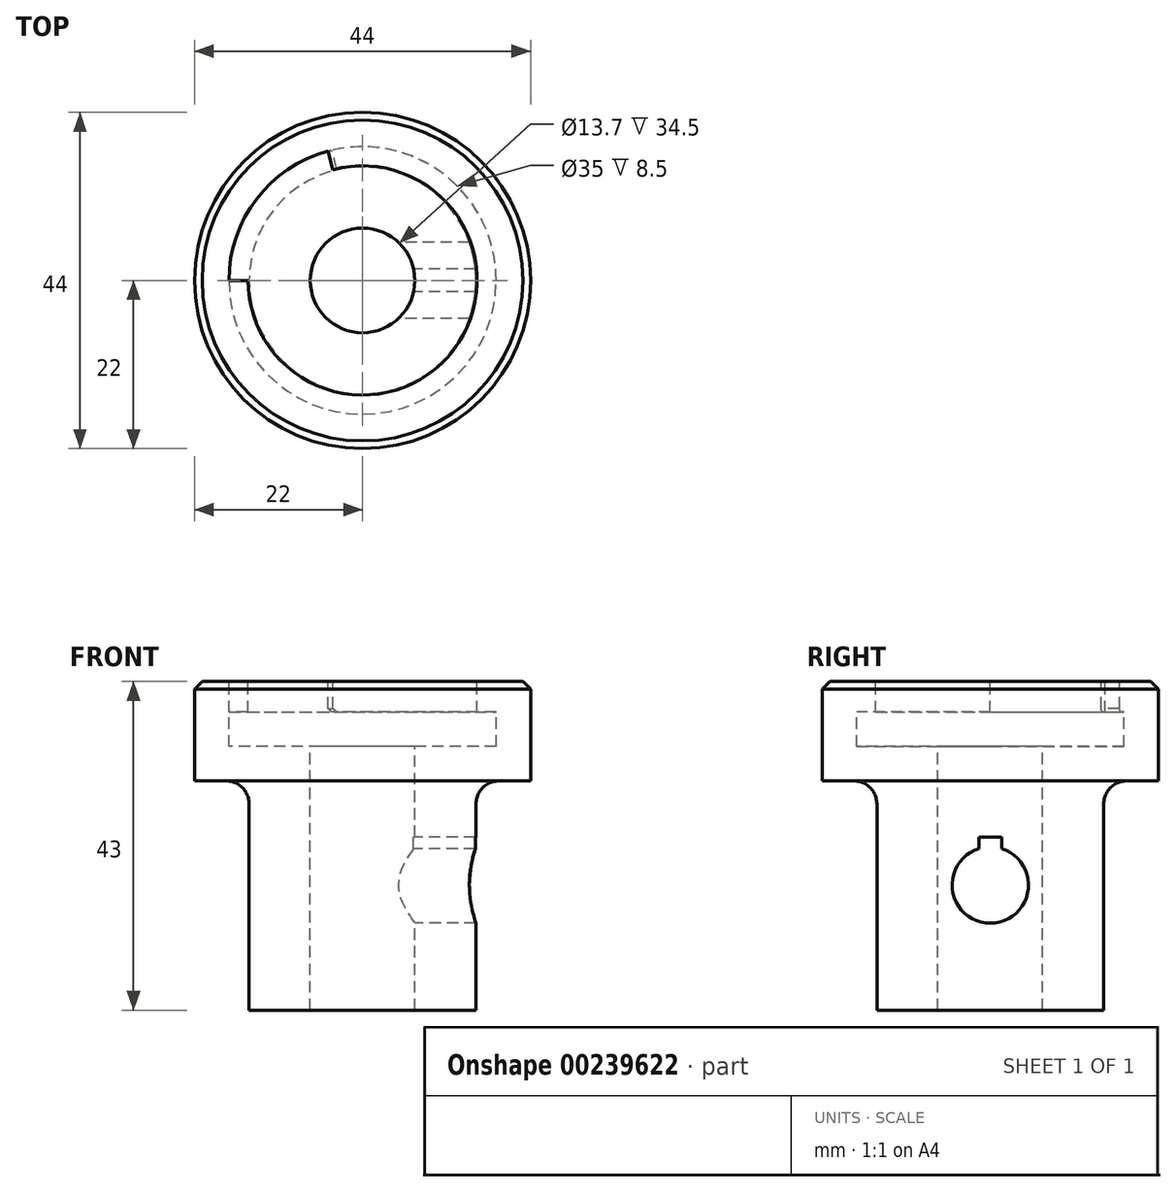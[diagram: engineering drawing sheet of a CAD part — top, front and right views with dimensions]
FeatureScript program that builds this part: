
annotation { "Feature Type Name" : "Feature", "Feature Type Description" : "" }
export const myFeature = defineFeature(function(context is Context, id is Id, definition is map)
    precondition{}
    {
        {
            var Q0;
            Q0=qCreatedBy(makeId("Front.planeOp"),FACE);
            var sketch = newSketch(context, id + "F0", { "sketchPlane" : qUnion([Q0])});
            skLineSegment(sketch, "E0", {"start": v(-22, 30) * mm, "end": v(-22, 43) * mm});
            skLineSegment(sketch, "E1", {"start": v(-22, 43) * mm, "end": v(-15, 43) * mm});
            skLineSegment(sketch, "E2", {"start": v(-15, 43) * mm, "end": v(-15, 39) * mm});
            skLineSegment(sketch, "E3", {"start": v(-15, 39) * mm, "end": v(-17.5, 39) * mm});
            skLineSegment(sketch, "E4", {"start": v(-17.5, 39) * mm, "end": v(-17.5, 34.5) * mm});
            skLineSegment(sketch, "E5", {"start": v(-17.5, 34.5) * mm, "end": v(-6.85, 34.5) * mm});
            skLineSegment(sketch, "E6", {"start": v(-6.85, 34.5) * mm, "end": v(-6.85, 0) * mm});
            skLineSegment(sketch, "E7", {"start": v(0, 7.97) * mm, "end": v(0, -2.06) * mm});
            skLineSegment(sketch, "E8", {"start": v(-14.85, 0) * mm, "end": v(-6.85, 0) * mm});
            skLineSegment(sketch, "E9", {"start": v(-22, 30) * mm, "end": v(-17.85, 30) * mm});
            skLineSegment(sketch, "E10", {"start": v(-14.85, 27) * mm, "end": v(-14.85, 0) * mm});
            skPoint(sketch, "E11.visualSharp", {"position": v(-14.85, 30) * mm});
            skArc(sketch, "E11.filletArc", {"start": v(-14.85, 27) * mm, "mid": v(-15.73, 29.12) * mm, "end": v(-17.85, 30) * mm});
            skSolve(sketch);
        }
        {
            var Q0;
            Q0 = qSketchRegion(id + "F0", true);
            var Q1;
            Q1=sQuery(id+"F0.wireOp",EDGE,"E7");
            revolve(context, id + "F1", {"entities" : qUnion([Q0]), "axis" : qUnion([Q1]), "revolveType" : RevolveType.FULL});
        }
        {
            var Q0;
            Q0=makeQuery(id+"F1.opRevolve","SWEPT_FACE",FACE,{"disambiguationData":[OSD([sQuery(id+"F0.wireOp",EDGE,"E1")])]});
            var sketch = newSketch(context, id + "F2", { "sketchPlane" : qUnion([Q0])});
            skCircle(sketch, "E12", {"center": v(0, 0) * mm, "radius": 17.5 * mm});
            skLineSegment(sketch, "E13", {"start": v(-15, 0) * mm, "end": v(-17.5, 0) * mm});
            skLineSegment(sketch, "E14", {"start": v(-3.88, 14.49) * mm, "end": v(-4.53, 16.9) * mm});
            skSolve(sketch);
        }
        {
            var Q0;
            {var subQ0=sQuery(id+"F2.wireOp",EDGE,"E13");Q0=makeQuery(id+"F2.imprint","IMPRINT",FACE,{"disambiguationData":[TD([[makeQuery(id+"F2.imprint","IMPRINT",EDGE,{"derivedFrom":subQ0}),-1.0]])]});}
            extrude(context, id + "F3", {"entities" : qUnion([Q0]), "operationType" : NewBodyOperationType.REMOVE, "oppositeDirection" : true, "depth" : 4.5 * mm});
        }
        {
            var Q0;
            Q0=makeQuery(id+"F1.opRevolve","SWEPT_EDGE",EDGE,{"disambiguationData":[OSD([sQuery(id+"F0.wireOp",EDGE,"E0"),sQuery(id+"F0.wireOp",EDGE,"E1")])]});
            chamfer(context, id + "F4", {"entities" : qUnion([Q0]), "width" : 1 * mm, "tangentPropagation" : true});
        }
        {
            var Q0;
            {var subQ0=sQuery(id+"F2.wireOp",EDGE,"E14");Q0=makeQuery(id+"Fz9Qw8WGeFSAcPO_1.2.F3.boolean.opBoolean","INTERSECT",EDGE,{"derivedFrom":[makeQuery(id+"Fz9Qw8WGeFSAcPO_1.1.F3.boolean.opBoolean","SPLIT",FACE,{"disambiguationData":[TD([makeQuery(id+"F3.boolean.opBoolean","COPY",FACE,{"derivedFrom":makeQuery(id+"F3.opExtrude","SWEPT_FACE",FACE,{"disambiguationData":[OSD([subQ0])]})})])],"derivedFrom":makeQuery(id+"F1.opRevolve","SWEPT_FACE",FACE,{"disambiguationData":[OSD([sQuery(id+"F0.wireOp",EDGE,"E3")])]})}),makeQuery(id+"Fz9Qw8WGeFSAcPO_1.2.F3.opExtrude","SWEPT_FACE",FACE,{"disambiguationData":[OSD([subQ0])]})]});}
            var Q1;
            {var subQ0=sQuery(id+"F2.wireOp",EDGE,"E14");var subQ1=makeQuery(id+"F3.boolean.opBoolean","COPY",FACE,{"derivedFrom":makeQuery(id+"F3.opExtrude","SWEPT_FACE",FACE,{"disambiguationData":[OSD([subQ0])]})});Q1=makeQuery(id+"Fz9Qw8WGeFSAcPO_1.3.F3.boolean.opBoolean","INTERSECT",EDGE,{"derivedFrom":[makeQuery(id+"Fz9Qw8WGeFSAcPO_1.2.F3.boolean.opBoolean","SPLIT",FACE,{"disambiguationData":[TD([subQ1])],"derivedFrom":makeQuery(id+"Fz9Qw8WGeFSAcPO_1.1.F3.boolean.opBoolean","SPLIT",FACE,{"disambiguationData":[TD([subQ1])],"derivedFrom":makeQuery(id+"F1.opRevolve","SWEPT_FACE",FACE,{"disambiguationData":[OSD([sQuery(id+"F0.wireOp",EDGE,"E3")])]})})}),makeQuery(id+"Fz9Qw8WGeFSAcPO_1.3.F3.opExtrude","SWEPT_FACE",FACE,{"disambiguationData":[OSD([subQ0])]})]});}
            var Q2;
            Q2=makeQuery(id+"F3.boolean.opBoolean","INTERSECT",EDGE,{"derivedFrom":[makeQuery(id+"F1.opRevolve","SWEPT_FACE",FACE,{"disambiguationData":[OSD([sQuery(id+"F0.wireOp",EDGE,"E3")])]}),makeQuery(id+"F3.opExtrude","SWEPT_FACE",FACE,{"disambiguationData":[OSD([sQuery(id+"F2.wireOp",EDGE,"E14")])]})]});
            var Q3;
            Q3=makeQuery(id+"Fz9Qw8WGeFSAcPO_1.1.F3.boolean.opBoolean","INTERSECT",EDGE,{"derivedFrom":[makeQuery(id+"F1.opRevolve","SWEPT_FACE",FACE,{"disambiguationData":[OSD([sQuery(id+"F0.wireOp",EDGE,"E3")])]}),makeQuery(id+"Fz9Qw8WGeFSAcPO_1.1.F3.opExtrude","SWEPT_FACE",FACE,{"disambiguationData":[OSD([sQuery(id+"F2.wireOp",EDGE,"E14")])]})]});
            chamfer(context, id + "F5", {"entities" : qUnion([Q0, Q1, Q2, Q3]), "width" : 0.5 * mm, "tangentPropagation" : true});
        }
        {
            var Q0;
            Q0=qCreatedBy(makeId("Right.planeOp"),FACE);
            var sketch = newSketch(context, id + "F6", { "sketchPlane" : qUnion([Q0])});
            skCircle(sketch, "E15", {"center": v(0, 16.37) * mm, "radius": 5 * mm});
            skSolve(sketch);
        }
        {
            var Q0;
            Q0 = qSketchRegion(id + "F6", true);
            extrude(context, id + "F7", {"entities" : qUnion([Q0]), "operationType" : NewBodyOperationType.REMOVE, "endBound" : BoundingType.THROUGH_ALL, "depth" : 25 * mm});
        }
        {
            var Q0;
            Q0=qCreatedBy(makeId("Right.planeOp"),FACE);
            var sketch = newSketch(context, id + "F8", { "sketchPlane" : qUnion([Q0])});
            skLineSegment(sketch, "E16", {"start": v(-1.5, 21.14) * mm, "end": v(-1.5, 22.64) * mm});
            skLineSegment(sketch, "E17", {"start": v(-1.5, 22.64) * mm, "end": v(1.5, 22.64) * mm});
            skLineSegment(sketch, "E18", {"start": v(1.5, 22.64) * mm, "end": v(1.5, 21.14) * mm});
            skLineSegment(sketch, "E19", {"start": v(-1.5, 21.14) * mm, "end": v(1.5, 21.14) * mm});
            skSolve(sketch);
        }
        {
            var Q0;
            Q0 = qSketchRegion(id + "F8", true);
            extrude(context, id + "F9", {"entities" : qUnion([Q0]), "operationType" : NewBodyOperationType.REMOVE, "endBound" : BoundingType.THROUGH_ALL, "depth" : 25 * mm});
        }
    });
